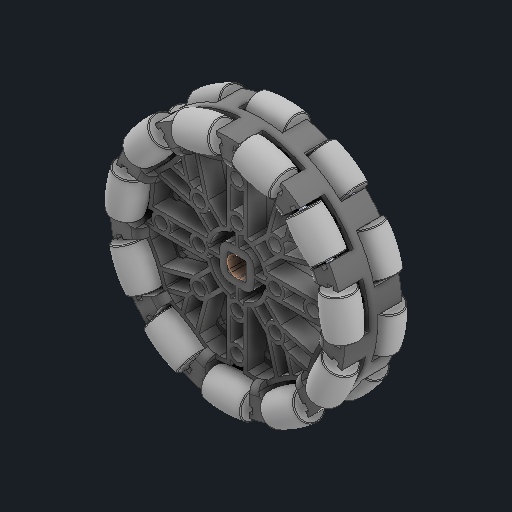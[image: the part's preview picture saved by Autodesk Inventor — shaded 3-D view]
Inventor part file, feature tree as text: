
AUTODESK INVENTOR PART (.ipt)
format: ipt  version: 2024 (Build 280153000, 153)  size: 3,338,240 bytes
history: native  units: in
note: dims shown in document units (in); Inventor stores cm internally (conversion verified against a paired STEP export)
features: other x49, sketch x1
ambient origin geometry x8: Origin, YZ Plane, XZ Plane, XY Plane, X Axis, Y Axis, Z Axis, Center Point
bodies: Solid1 (feature_tree), Solid2 (feature_tree), Solid3 (feature_tree), Solid4 (feature_tree), Solid5 (feature_tree), Solid6 (feature_tree), Solid7 (feature_tree), Solid8 (feature_tree), Solid9 (feature_tree), Solid10 (feature_tree), Solid11 (feature_tree), Solid12 (feature_tree), Solid13 (feature_tree), Solid14 (feature_tree), Solid15 (feature_tree), Solid16 (feature_tree), Solid17 (feature_tree), Solid18 (feature_tree), Solid19 (feature_tree), Solid20 (feature_tree), Solid21 (feature_tree), Solid22 (feature_tree), Solid23 (feature_tree), Solid24 (feature_tree), Solid25 (feature_tree), Solid26 (feature_tree), Solid27 (feature_tree), Solid28 (feature_tree), Solid29 (feature_tree), Solid30 (feature_tree), Solid31 (feature_tree), Solid32 (feature_tree), Solid33 (feature_tree), Solid34 (feature_tree), Solid35 (feature_tree), Solid36 (feature_tree), Solid37 (feature_tree), Solid38 (feature_tree), Solid39 (feature_tree), Solid40 (feature_tree), Solid41 (feature_tree), Solid42 (feature_tree), Solid43 (feature_tree), Solid44 (feature_tree), Solid45 (feature_tree)
feature tree (50):
  other  "3.25 Omni Antistatic.ipt"
  other  "Solid1::3.25 Omni Antistatic.ipt"
  other  "Solid2::3.25 Omni Antistatic.ipt"
  other  "Solid3::3.25 Omni Antistatic.ipt"
  other  "Solid4::3.25 Omni Antistatic.ipt"
  other  "Solid5::3.25 Omni Antistatic.ipt"
  other  "Solid6::3.25 Omni Antistatic.ipt"
  other  "Solid7::3.25 Omni Antistatic.ipt"
  other  "Solid8::3.25 Omni Antistatic.ipt"
  other  "Solid9::3.25 Omni Antistatic.ipt"
  other  "Solid10::3.25 Omni Antistatic.ipt"
  other  "Solid11::3.25 Omni Antistatic.ipt"
  other  "Solid12::3.25 Omni Antistatic.ipt"
  other  "Solid13::3.25 Omni Antistatic.ipt"
  other  "Solid14::3.25 Omni Antistatic.ipt"
  other  "Solid15::3.25 Omni Antistatic.ipt"
  other  "Solid16::3.25 Omni Antistatic.ipt"
  other  "Solid17::3.25 Omni Antistatic.ipt"
  other  "Solid18::3.25 Omni Antistatic.ipt"
  other  "Solid19::3.25 Omni Antistatic.ipt"
  other  "Solid20::3.25 Omni Antistatic.ipt"
  other  "Solid21::3.25 Omni Antistatic.ipt"
  other  "Solid22::3.25 Omni Antistatic.ipt"
  other  "Solid23::3.25 Omni Antistatic.ipt"
  other  "Solid24::3.25 Omni Antistatic.ipt"
  other  "Solid25::3.25 Omni Antistatic.ipt"
  other  "Solid26::3.25 Omni Antistatic.ipt"
  other  "Solid27::3.25 Omni Antistatic.ipt"
  other  "Solid28::3.25 Omni Antistatic.ipt"
  other  "Solid29::3.25 Omni Antistatic.ipt"
  other  "Solid30::3.25 Omni Antistatic.ipt"
  other  "Solid31::3.25 Omni Antistatic.ipt"
  other  "Solid32::3.25 Omni Antistatic.ipt"
  other  "Solid33::3.25 Omni Antistatic.ipt"
  other  "Solid34::3.25 Omni Antistatic.ipt"
  other  "Solid35::3.25 Omni Antistatic.ipt"
  other  "Solid36::3.25 Omni Antistatic.ipt"
  other  "Solid37::3.25 Omni Antistatic.ipt"
  other  "Solid38::3.25 Omni Antistatic.ipt"
  other  "Solid39::3.25 Omni Antistatic.ipt"
  other  "Solid40::3.25 Omni Antistatic.ipt"
  other  "Solid41::3.25 Omni Antistatic.ipt"
  other  "Solid42::3.25 Omni Antistatic.ipt"
  other  "Solid43::3.25 Omni Antistatic.ipt"
  other  "Solid44::3.25 Omni Antistatic.ipt"
  other  "Solid45::3.25 Omni Antistatic.ipt"
  other  "TaggingFeature1"
  sketch  "Sketch1"  dims[d0=0.3937in]
  other  "Srf1"
  other  "Srf1::Derived"
